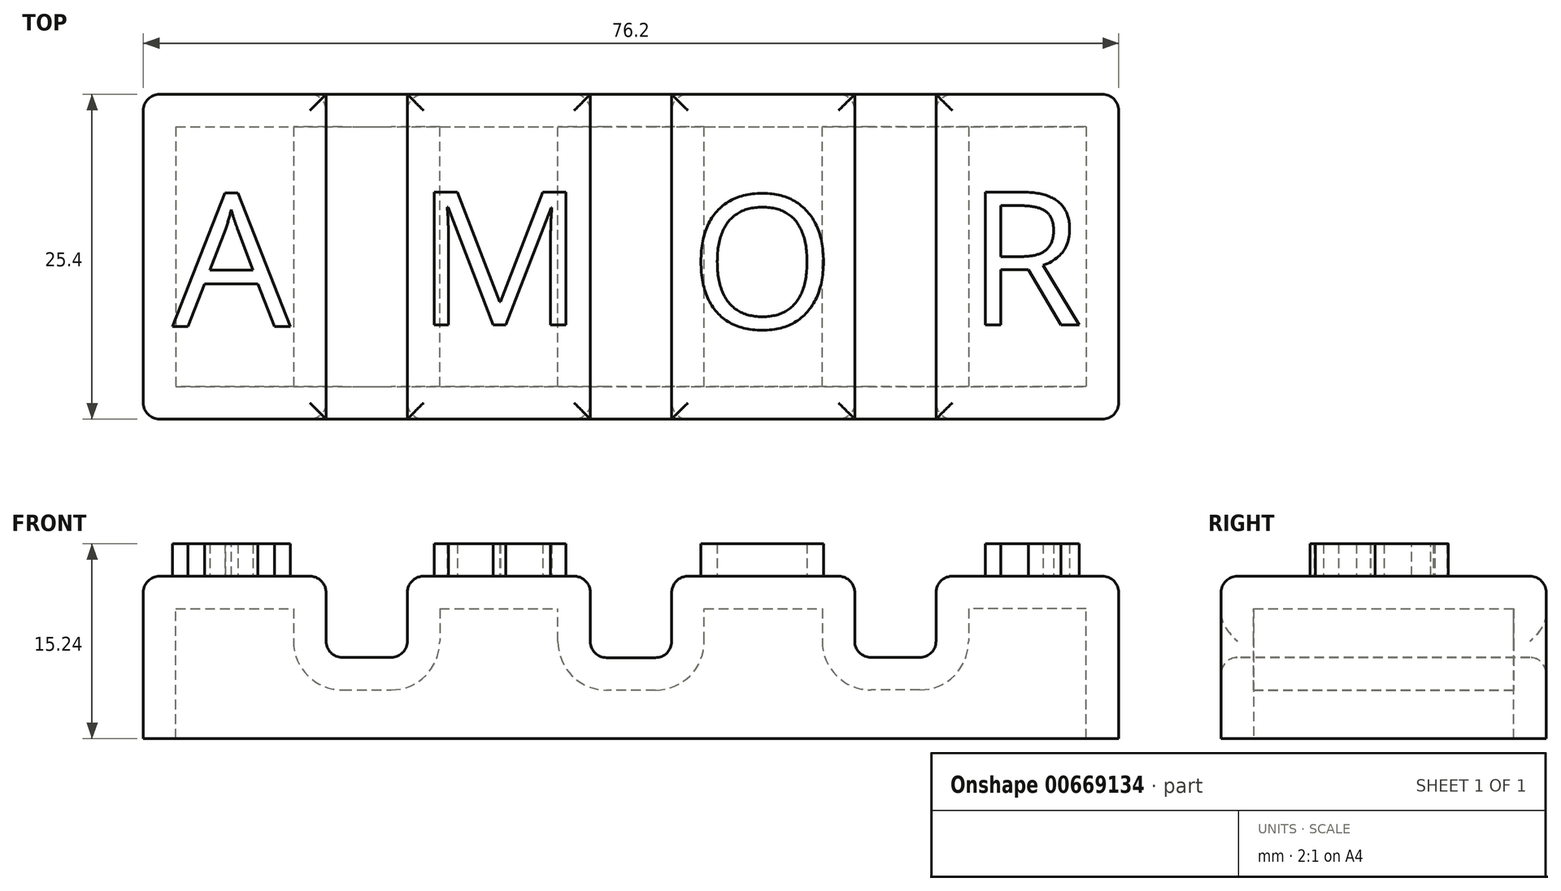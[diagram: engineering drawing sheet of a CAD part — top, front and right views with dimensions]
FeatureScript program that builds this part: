
annotation { "Feature Type Name" : "Feature", "Feature Type Description" : "" }
export const myFeature = defineFeature(function(context is Context, id is Id, definition is map)
    precondition{}
    {
        {
            var Q0;
            Q0=qCreatedBy(makeId("Top.planeOp"),FACE);
            var sketch = newSketch(context, id + "F0", { "sketchPlane" : qUnion([Q0])});
            skLineSegment(sketch, "E0.bottom", {"start": v(-38.1, 12.7) * mm, "end": v(38.1, 12.7) * mm});
            skLineSegment(sketch, "E0.top", {"start": v(-38.1, -12.7) * mm, "end": v(38.1, -12.7) * mm});
            skLineSegment(sketch, "E0.left", {"start": v(-38.1, 12.7) * mm, "end": v(-38.1, -12.7) * mm});
            skLineSegment(sketch, "E0.right", {"start": v(38.1, 12.7) * mm, "end": v(38.1, -12.7) * mm});
            skPoint(sketch, "E0.middle", {"position": v(0, 0) * mm});
            skSolve(sketch);
        }
        {
            var Q0;
            Q0 = qSketchRegion(id + "F0", true);
            extrude(context, id + "F1", {"entities" : qUnion([Q0]), "depth" : 12.7 * mm, "offsetDistance" : 25.4 * mm});
        }
        {
            var Q0;
            Q0=makeQuery(id+"F1.opExtrude","SWEPT_FACE",FACE,{"disambiguationData":[OSD([sQuery(id+"F0.wireOp",EDGE,"E0.top")])]});
            var sketch = newSketch(context, id + "F2", { "sketchPlane" : qUnion([Q0])});
            skLineSegment(sketch, "E1", {"start": v(-38.1, 6.35) * mm, "end": v(38.1, 6.35) * mm, "construction": true});
            skPoint(sketch, "E2.middle", {"position": v(0, 12.7) * mm});
            skPoint(sketch, "E3.middle", {"position": v(20.65, 12.7) * mm});
            skPoint(sketch, "E4.middle", {"position": v(-20.65, 12.7) * mm});
            skLineSegment(sketch, "E5.bottom", {"start": v(-3.18, 19.07) * mm, "end": v(3.17, 19.07) * mm});
            skLineSegment(sketch, "E5.top", {"start": v(-3.18, 6.33) * mm, "end": v(3.17, 6.33) * mm});
            skLineSegment(sketch, "E5.left", {"start": v(-3.18, 19.07) * mm, "end": v(-3.18, 6.33) * mm});
            skLineSegment(sketch, "E5.right", {"start": v(3.17, 19.07) * mm, "end": v(3.17, 6.33) * mm});
            skLineSegment(sketch, "E6.bottom", {"start": v(-17.48, 6.35) * mm, "end": v(-23.83, 6.35) * mm});
            skLineSegment(sketch, "E6.top", {"start": v(-17.48, 19.05) * mm, "end": v(-23.83, 19.05) * mm});
            skLineSegment(sketch, "E6.left", {"start": v(-17.48, 6.35) * mm, "end": v(-17.48, 19.05) * mm});
            skLineSegment(sketch, "E6.right", {"start": v(-23.83, 6.35) * mm, "end": v(-23.83, 19.05) * mm});
            skLineSegment(sketch, "E7.bottom", {"start": v(17.48, 6.35) * mm, "end": v(23.83, 6.35) * mm});
            skLineSegment(sketch, "E7.top", {"start": v(17.48, 19.05) * mm, "end": v(23.83, 19.05) * mm});
            skLineSegment(sketch, "E7.left", {"start": v(17.48, 6.35) * mm, "end": v(17.48, 19.05) * mm});
            skLineSegment(sketch, "E7.right", {"start": v(23.83, 6.35) * mm, "end": v(23.83, 19.05) * mm});
            skSolve(sketch);
        }
        {
            var Q0;
            Q0 = qSketchRegion(id + "F2", true);
            extrude(context, id + "F3", {"entities" : qUnion([Q0]), "operationType" : NewBodyOperationType.REMOVE, "endBound" : BoundingType.THROUGH_ALL, "oppositeDirection" : true, "depth" : 25.4 * mm, "offsetDistance" : 25.4 * mm});
        }
        {
            var Q0;
            {var subQ0=sQuery(id+"F0.wireOp",EDGE,"E0.bottom");var subQ1=sQuery(id+"F0.wireOp",EDGE,"E0.top");var subQ2=sQuery(id+"F0.wireOp",EDGE,"E0.left");Q0=makeQuery(id+"F3.boolean.opBoolean","SPLIT",FACE,{"disambiguationData":[TD([makeQuery(id+"F1.opExtrude","SWEPT_FACE",FACE,{"disambiguationData":[OSD([subQ2])]})])],"derivedFrom":makeQuery(id+"F1.opExtrude","CAP_FACE",FACE,{"disambiguationData":[OSD([subQ0,subQ1,subQ2,sQuery(id+"F0.wireOp",EDGE,"E0.right")])],"isStart":false})});}
            var Q1;
            Q1=makeQuery(id+"F3.boolean.opBoolean","INTERSECT",EDGE,{"derivedFrom":[makeQuery(id+"F1.opExtrude","CAP_FACE",FACE,{"disambiguationData":[OSD([sQuery(id+"F0.wireOp",EDGE,"E0.bottom"),sQuery(id+"F0.wireOp",EDGE,"E0.top"),sQuery(id+"F0.wireOp",EDGE,"E0.left"),sQuery(id+"F0.wireOp",EDGE,"E0.right")])],"isStart":false}),makeQuery(id+"F3.opExtrude","SWEPT_FACE",FACE,{"disambiguationData":[OSD([sQuery(id+"F2.wireOp",EDGE,"E5.left")])]})]});
            var Q2;
            {var subQ0=sQuery(id+"F0.wireOp",EDGE,"E0.bottom");var subQ1=sQuery(id+"F0.wireOp",EDGE,"E0.top");Q2=makeQuery(id+"F3.boolean.opBoolean","SPLIT",FACE,{"disambiguationData":[TD([makeQuery(id+"F3.opExtrude","SWEPT_FACE",FACE,{"disambiguationData":[OSD([sQuery(id+"F2.wireOp",EDGE,"E5.left")])]})])],"derivedFrom":makeQuery(id+"F1.opExtrude","CAP_FACE",FACE,{"disambiguationData":[OSD([subQ0,subQ1,sQuery(id+"F0.wireOp",EDGE,"E0.left"),sQuery(id+"F0.wireOp",EDGE,"E0.right")])],"isStart":false})});}
            var Q3;
            {var subQ0=sQuery(id+"F0.wireOp",EDGE,"E0.bottom");var subQ1=sQuery(id+"F0.wireOp",EDGE,"E0.top");Q3=makeQuery(id+"F3.boolean.opBoolean","SPLIT",FACE,{"disambiguationData":[TD([makeQuery(id+"F3.opExtrude","SWEPT_FACE",FACE,{"disambiguationData":[OSD([sQuery(id+"F2.wireOp",EDGE,"E5.right")])]})])],"derivedFrom":makeQuery(id+"F1.opExtrude","CAP_FACE",FACE,{"disambiguationData":[OSD([subQ0,subQ1,sQuery(id+"F0.wireOp",EDGE,"E0.left"),sQuery(id+"F0.wireOp",EDGE,"E0.right")])],"isStart":false})});}
            var Q4;
            {var subQ0=sQuery(id+"F0.wireOp",EDGE,"E0.bottom");var subQ1=sQuery(id+"F0.wireOp",EDGE,"E0.right");var subQ2=sQuery(id+"F0.wireOp",EDGE,"E0.top");Q4=makeQuery(id+"F3.boolean.opBoolean","SPLIT",FACE,{"disambiguationData":[TD([makeQuery(id+"F1.opExtrude","SWEPT_FACE",FACE,{"disambiguationData":[OSD([subQ1])]})])],"derivedFrom":makeQuery(id+"F1.opExtrude","CAP_FACE",FACE,{"disambiguationData":[OSD([subQ0,subQ2,sQuery(id+"F0.wireOp",EDGE,"E0.left"),subQ1])],"isStart":false})});}
            var Q5;
            Q5=makeQuery(id+"F3.boolean.opBoolean","COPY",FACE,{"derivedFrom":makeQuery(id+"F3.opExtrude","SWEPT_FACE",FACE,{"disambiguationData":[OSD([sQuery(id+"F2.wireOp",EDGE,"E6.bottom")])]})});
            var Q6;
            Q6=makeQuery(id+"F3.boolean.opBoolean","COPY",FACE,{"derivedFrom":makeQuery(id+"F3.opExtrude","SWEPT_FACE",FACE,{"disambiguationData":[OSD([sQuery(id+"F2.wireOp",EDGE,"E5.top")])]})});
            var Q7;
            Q7=makeQuery(id+"F3.boolean.opBoolean","COPY",FACE,{"derivedFrom":makeQuery(id+"F3.opExtrude","SWEPT_FACE",FACE,{"disambiguationData":[OSD([sQuery(id+"F2.wireOp",EDGE,"E7.bottom")])]})});
            var Q8;
            Q8=makeQuery(id+"F1.opExtrude","SWEPT_EDGE",EDGE,{"disambiguationData":[OSD([sQuery(id+"F0.wireOp",EDGE,"E0.top"),sQuery(id+"F0.wireOp",EDGE,"E0.right")])]});
            var Q9;
            Q9=makeQuery(id+"F1.opExtrude","SWEPT_EDGE",EDGE,{"disambiguationData":[OSD([sQuery(id+"F0.wireOp",EDGE,"E0.bottom"),sQuery(id+"F0.wireOp",EDGE,"E0.right")])]});
            var Q10;
            Q10=makeQuery(id+"F1.opExtrude","SWEPT_EDGE",EDGE,{"disambiguationData":[OSD([sQuery(id+"F0.wireOp",EDGE,"E0.top"),sQuery(id+"F0.wireOp",EDGE,"E0.left")])]});
            var Q11;
            Q11=makeQuery(id+"F1.opExtrude","SWEPT_EDGE",EDGE,{"disambiguationData":[OSD([sQuery(id+"F0.wireOp",EDGE,"E0.bottom"),sQuery(id+"F0.wireOp",EDGE,"E0.left")])]});
            fillet(context, id + "F4", {"entities" : qUnion([Q0, Q1, Q2, Q3, Q4, Q5, Q6, Q7, Q8, Q9, Q10, Q11]), "radius" : 1.27 * mm, "tangentPropagation" : true, "allowEdgeOverflow" : false});
        }
        {
            var Q0;
            Q0=makeQuery(id+"F1.opExtrude","CAP_FACE",FACE,{"disambiguationData":[OSD([sQuery(id+"F0.wireOp",EDGE,"E0.bottom"),sQuery(id+"F0.wireOp",EDGE,"E0.top"),sQuery(id+"F0.wireOp",EDGE,"E0.left"),sQuery(id+"F0.wireOp",EDGE,"E0.right")])],"isStart":true});
            shell(context, id + "F5", {"entities" : qUnion([Q0]), "thickness" : 2.54 * mm});
        }
        {
            var Q0;
            {var subQ0=sQuery(id+"F0.wireOp",EDGE,"E0.bottom");var subQ1=sQuery(id+"F0.wireOp",EDGE,"E0.top");Q0=makeQuery(id+"F3.boolean.opBoolean","SPLIT",FACE,{"disambiguationData":[TD([makeQuery(id+"F3.opExtrude","SWEPT_FACE",FACE,{"disambiguationData":[OSD([sQuery(id+"F2.wireOp",EDGE,"E5.left")])]})])],"derivedFrom":makeQuery(id+"F1.opExtrude","CAP_FACE",FACE,{"disambiguationData":[OSD([subQ0,subQ1,sQuery(id+"F0.wireOp",EDGE,"E0.left"),sQuery(id+"F0.wireOp",EDGE,"E0.right")])],"isStart":false})});}
            var sketch = newSketch(context, id + "F6", { "sketchPlane" : qUnion([Q0])});
            skText(sketch, "E8", { "text": "A", "fontName": "OpenSans-Regular.ttf"});
            const initialGuessF6  = {"E8": [-0.03583, -0.00545, 1, 0, 0.01049]};
            skSetInitialGuess(sketch, initialGuessF6);
            skSolve(sketch);
        }
        {
            var Q0;
            {var subQ0=sQuery(id+"F0.wireOp",EDGE,"E0.bottom");var subQ2=sQuery(id+"F0.wireOp",EDGE,"E0.top");var subQ4=makeQuery(id+"F3.opExtrude","SWEPT_FACE",FACE,{"disambiguationData":[OSD([sQuery(id+"F2.wireOp",EDGE,"E5.left")])]});var subQ6=makeQuery(id+"F1.opExtrude","CAP_FACE",FACE,{"disambiguationData":[OSD([subQ0,subQ2,sQuery(id+"F0.wireOp",EDGE,"E0.left"),sQuery(id+"F0.wireOp",EDGE,"E0.right")])],"isStart":false});var subQ7=makeQuery(id+"F3.boolean.opBoolean","SPLIT",FACE,{"disambiguationData":[TD([subQ4])],"derivedFrom":subQ6});Q0=makeQuery(id+"F6.imprint","IMPRINT",FACE,{"disambiguationData":[TD([[makeQuery(id+"F6.imprint","IMPRINT",EDGE,{"derivedFrom":makeQuery(id+"F4.opFillet","BLEND_EDGE",EDGE,{"blendedFrom":[makeQuery(id+"F3.boolean.opBoolean","INTERSECT",EDGE,{"derivedFrom":[subQ6,subQ4]}),subQ7],"blendedInto":[subQ7]})}),1.0]])]});}
            var sketch = newSketch(context, id + "F7", { "sketchPlane" : qUnion([Q0])});
            skText(sketch, "E9", { "text": "M", "fontName": "OpenSans-Regular.ttf"});
            const initialGuessF7  = {"E9": [-0.01681, -0.00535, 1, 0, 0.01049]};
            skSetInitialGuess(sketch, initialGuessF7);
            skSolve(sketch);
        }
        {
            var Q0;
            {var subQ0=sQuery(id+"F0.wireOp",EDGE,"E0.bottom");var subQ1=sQuery(id+"F0.wireOp",EDGE,"E0.top");Q0=makeQuery(id+"F3.boolean.opBoolean","SPLIT",FACE,{"disambiguationData":[TD([makeQuery(id+"F3.opExtrude","SWEPT_FACE",FACE,{"disambiguationData":[OSD([sQuery(id+"F2.wireOp",EDGE,"E5.right")])]})])],"derivedFrom":makeQuery(id+"F1.opExtrude","CAP_FACE",FACE,{"disambiguationData":[OSD([subQ0,subQ1,sQuery(id+"F0.wireOp",EDGE,"E0.left"),sQuery(id+"F0.wireOp",EDGE,"E0.right")])],"isStart":false})});}
            var sketch = newSketch(context, id + "F8", { "sketchPlane" : qUnion([Q0])});
            skText(sketch, "E10", { "text": "O", "fontName": "OpenSans-Regular.ttf"});
            const initialGuessF8  = {"E10": [0.00457, -0.00561, 1, 0, 0.01049]};
            skSetInitialGuess(sketch, initialGuessF8);
            skSolve(sketch);
        }
        {
            var Q0;
            {var subQ0=sQuery(id+"F0.wireOp",EDGE,"E0.bottom");var subQ1=sQuery(id+"F0.wireOp",EDGE,"E0.right");var subQ2=sQuery(id+"F0.wireOp",EDGE,"E0.top");Q0=makeQuery(id+"F3.boolean.opBoolean","SPLIT",FACE,{"disambiguationData":[TD([makeQuery(id+"F1.opExtrude","SWEPT_FACE",FACE,{"disambiguationData":[OSD([subQ1])]})])],"derivedFrom":makeQuery(id+"F1.opExtrude","CAP_FACE",FACE,{"disambiguationData":[OSD([subQ0,subQ2,sQuery(id+"F0.wireOp",EDGE,"E0.left"),subQ1])],"isStart":false})});}
            var sketch = newSketch(context, id + "F9", { "sketchPlane" : qUnion([Q0])});
            skText(sketch, "E11", { "text": "R", "fontName": "OpenSans-Regular.ttf"});
            const initialGuessF9  = {"E11": [0.02624, -0.00535, 1, 0, 0.01049]};
            skSetInitialGuess(sketch, initialGuessF9);
            skSolve(sketch);
        }
        {
            var Q0;
            Q0 = qSketchRegion(id + "F6", true);
            extrude(context, id + "F10", {"entities" : qUnion([Q0]), "operationType" : NewBodyOperationType.ADD, "depth" : 2.54 * mm, "offsetDistance" : 25.4 * mm});
        }
        {
            var Q0;
            Q0 = qSketchRegion(id + "F7", true);
            extrude(context, id + "F11", {"entities" : qUnion([Q0]), "operationType" : NewBodyOperationType.ADD, "depth" : 2.54 * mm, "offsetDistance" : 25.4 * mm});
        }
        {
            var Q0;
            Q0 = qSketchRegion(id + "F8", true);
            extrude(context, id + "F12", {"entities" : qUnion([Q0]), "operationType" : NewBodyOperationType.ADD, "depth" : 2.54 * mm, "offsetDistance" : 25.4 * mm});
        }
        {
            var Q0;
            Q0 = qSketchRegion(id + "F9", true);
            extrude(context, id + "F13", {"entities" : qUnion([Q0]), "operationType" : NewBodyOperationType.ADD, "depth" : 2.54 * mm, "offsetDistance" : 25.4 * mm});
        }
    });
